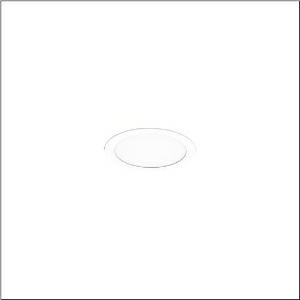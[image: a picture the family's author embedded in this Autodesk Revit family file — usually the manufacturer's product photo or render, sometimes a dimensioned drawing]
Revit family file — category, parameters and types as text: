
# Revit family: lunis_21_m_51db16tc91c
name_source: partatom
category: Lighting Fixtures
units: mm (PartAtom-declared; Revit-internal decimal feet)

## family parameters
Cut with Voids When Loaded = No
Host = Face
Light Source = No
Part Type = Normal
Room Calculation Point = No
Round Connector Dimension = Use Diameter
Shared = No

## types (1)
- --- (1 x LED 3000 K ... 6500 K, 3170 lm, 25.5 W, 4000K)
    Apparent Load = 26 VA
    CIE Flux Codes = 50 80 96 100 100
    Color Rendering = 80
    Color Temperature = 4000K
    Default Elevation = 1800 mm
    Description = Lunis 21,  M, downlight, light control with lens, of PMMA, optical cover: cover panel, of PC, opal, light emission: direct distribution, LED rated luminous flux: 3.170lm, light colour: 8tw, with terminal, 5-pole, mains connection: 220..240V, AC/DC, 0/50..60Hz, housing, round, of diecast aluminium, traffic white (RAL 9016), diameter: 115mm, clamping range: 1..40mm, protection rating (complete): IP20, protection rating (on room side): IP54, insulation class (complete): insulation class II (safety insulation), certification: CE, impact resistance: IK03, packaging unit: 1 piece
    Height = 0 mm  [stored 0 ft]
    Lamp = 1 x LED 3000 K ... 6500 K
    Lamp Light Flux = 3170 lm
    Lamp Power = 25.5 W
    Lamp count = 1
    Length = 115 mm
    Luminous efficacy = 124 lm/W
    Manufacturer = Siteco
    ModVariant = No
    Model = 51DB16TC91C
    Mounting Place = Ceiling
    Mounting Type = Recessed
    Number of Poles = 1
    OnlyDefault = Yes
    Power Factor = 1
    Product Name = Lunis 21 M
    Product group = downlight
    ProductGroupID = 400
    Protection Class = Protection class II
    Protection Degree = IP 20
    RLX_Detail_Level = 1
    RLX_Emergency_Light_Flux = 0 lm
    RLX_Emergency_Type = 0
    RLX_Emergency_Type_DB = No
    RlxData = <blob elided: 10061 chars, md5=f2447861>
    Socket = socket
    Standby Power = 0 W
    System Light Flux = 3170 lm
    System Power = 26 W
    Type Comments = individual setting: CCT=4000K, colour temperature 4000K, luminous flux: 100 % | (ON | ON | OFF | OFF) | 700 mA
    Type Image = l_1290848.jpg
    URL = http://relux.com
    VarID = @adj_018404
    Voltage = 0 V
    Weight = 0.00 kg
    Width = 0 mm  [stored 0 ft]

note: [stored X ft] marks values corroborated as IEEE doubles in the binary element streams (Revit-internal decimal feet)

## geometry (parser evidence)
native form markers: Sweep x9
no freeform markers — native parametric forms only
